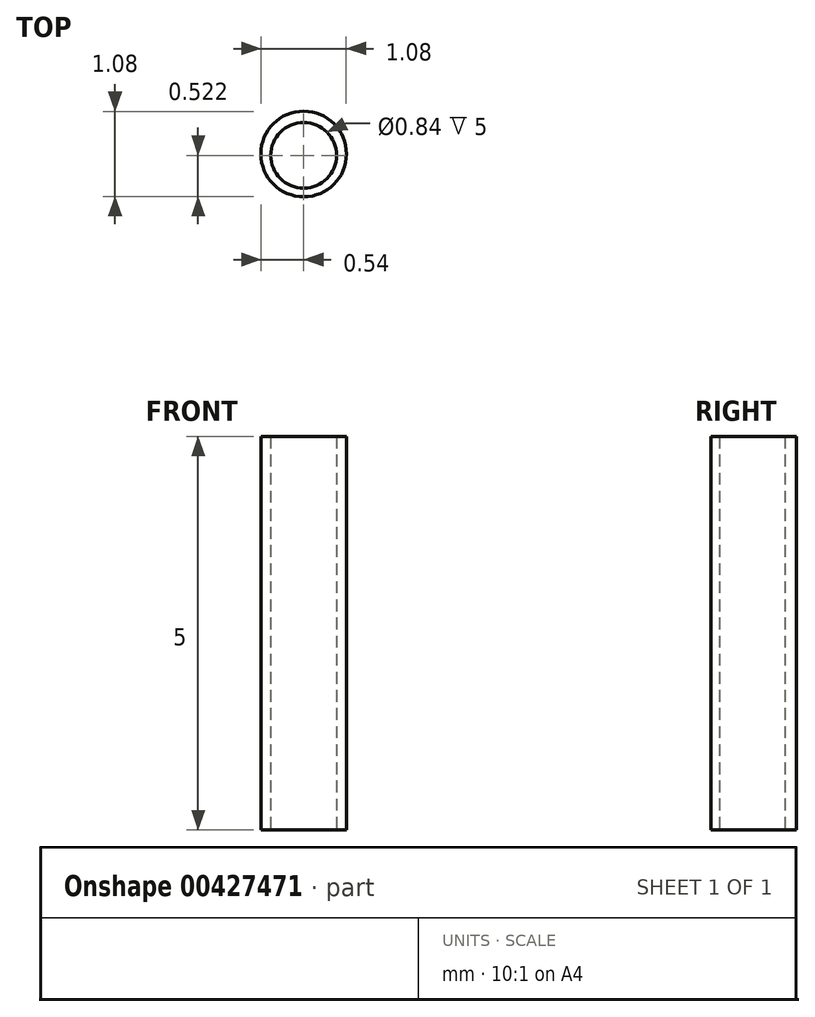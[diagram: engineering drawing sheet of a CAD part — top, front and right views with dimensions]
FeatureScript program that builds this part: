
annotation { "Feature Type Name" : "Feature", "Feature Type Description" : "" }
export const myFeature = defineFeature(function(context is Context, id is Id, definition is map)
    precondition{}
    {
        {
            var Q0;
            Q0=qCreatedBy(makeId("Top.planeOp"),FACE);
            var sketch = newSketch(context, id + "F0", { "sketchPlane" : qUnion([Q0])});
            skCircle(sketch, "E0", {"center": v(0, 0) * mm, "radius": 0.54 * mm});
            skCircle(sketch, "E1", {"center": v(0, -0.02) * mm, "radius": 0.42 * mm});
            skSolve(sketch);
        }
        {
            var Q0;
            Q0=makeQuery(id+"F0.imprint","IMPRINT",FACE,{"disambiguationData":[TD([[makeQuery(id+"F0.imprint","IMPRINT",EDGE,{"derivedFrom":sQuery(id+"F0.wireOp",EDGE,"E0")}),1.0]])]});
            extrude(context, id + "F1", {"entities" : qUnion([Q0]), "depth" : 5 * mm});
        }
    });
